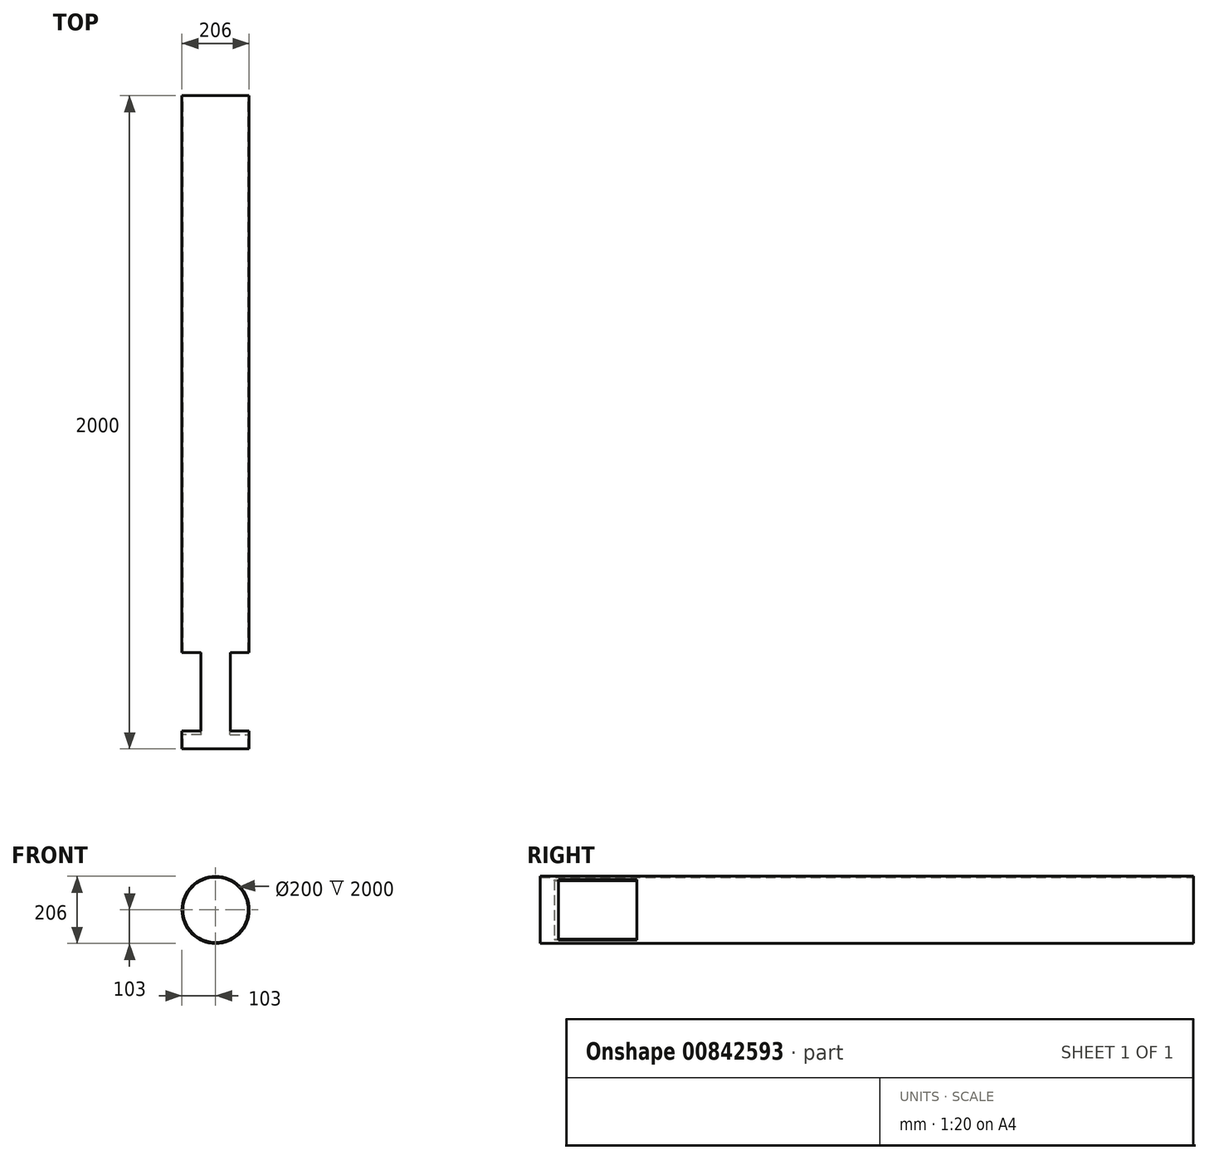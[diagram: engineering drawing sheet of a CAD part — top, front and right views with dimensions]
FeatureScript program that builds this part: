
annotation { "Feature Type Name" : "Feature", "Feature Type Description" : "" }
export const myFeature = defineFeature(function(context is Context, id is Id, definition is map)
    precondition{}
    {
        {
            var Q0;
            Q0=qCreatedBy(makeId("Front.planeOp"),FACE);
            var sketch = newSketch(context, id + "F0", { "sketchPlane" : qUnion([Q0])});
            skCircle(sketch, "E0", {"center": v(0, 0) * mm, "radius": 103 * mm});
            skCircle(sketch, "E1", {"center": v(0, 0) * mm, "radius": 100 * mm});
            skSolve(sketch);
        }
        {
            var Q0;
            Q0 = qSketchRegion(id + "F0", true);
            extrude(context, id + "F1", {"entities" : qUnion([Q0]), "depth" : 2000 * mm, "offsetDistance" : 25 * mm});
        }
        {
            var Q0;
            Q0=makeQuery(id+"F1.opExtrude","CAP_FACE",FACE,{"disambiguationData":[OSD([sQuery(id+"F0.wireOp",EDGE,"E0"),sQuery(id+"F0.wireOp",EDGE,"E1")])],"isStart":false});
            cPlane(context, id + "F2", {"entities" : qUnion([Q0]), "cplaneType" : CPlaneType.OFFSET, "offset" : 55 * mm, "oppositeDirection" : true, "width" : 150 * mm, "height" : 150 * mm});
        }
        {
            var Q0;
            Q0=qCreatedBy(id+"F2.planeOp",FACE);
            var sketch = newSketch(context, id + "F3", { "sketchPlane" : qUnion([Q0])});
            skArc(sketch, "E2", {"start": v(45.6, -93.47) * mm, "mid": v(104, 0) * mm, "end": v(45.6, 93.47) * mm});
            skArc(sketch, "E3.trimOffspring", {"start": v(-45.6, 93.47) * mm, "mid": v(-104, 0) * mm, "end": v(-45.6, -93.47) * mm});
            skLineSegment(sketch, "E4", {"start": v(-45.6, -93.47) * mm, "end": v(-14.63, -30) * mm});
            skLineSegment(sketch, "E5", {"start": v(45.6, -93.47) * mm, "end": v(14.63, -30) * mm});
            skLineSegment(sketch, "E6", {"start": v(-15.46, 31.7) * mm, "end": v(-45.6, 93.47) * mm});
            skLineSegment(sketch, "E7", {"start": v(15.46, 31.7) * mm, "end": v(45.6, 93.47) * mm});
            skLineSegment(sketch, "E8.bottom", {"start": v(15.46, 31.7) * mm, "end": v(-15.46, 31.7) * mm});
            skLineSegment(sketch, "E8.top", {"start": v(14.63, -30) * mm, "end": v(-14.63, -30) * mm});
            skPoint(sketch, "E8.middle", {"position": v(-0.41, 0.85) * mm});
            skSolve(sketch);
        }
        {
            var Q0;
            Q0 = qSketchRegion(id + "F3", true);
            extrude(context, id + "F4", {"entities" : qUnion([Q0]), "operationType" : NewBodyOperationType.REMOVE, "oppositeDirection" : true, "depth" : 240 * mm, "offsetDistance" : 25 * mm});
        }
        {
            var Q0;
            {var subQ0=sQuery(id+"F3.wireOp",EDGE,"E5");var subQ1=sQuery(id+"F3.wireOp",EDGE,"E7");Q0=makeQuery(id+"F4.boolean.opBoolean","COPY",FACE,{"disambiguationData":[TD([makeQuery(id+"F4.opExtrude","SWEPT_FACE",FACE,{"disambiguationData":[OSD([subQ0])]})])],"derivedFrom":makeQuery(id+"F4.opExtrude","CAP_FACE",FACE,{"disambiguationData":[OSD([sQuery(id+"F3.wireOp",EDGE,"E2"),sQuery(id+"F3.wireOp",EDGE,"E3.trimOffspring"),sQuery(id+"F3.wireOp",EDGE,"E4"),subQ0,sQuery(id+"F3.wireOp",EDGE,"E6"),subQ1,sQuery(id+"F3.wireOp",EDGE,"E8.bottom"),sQuery(id+"F3.wireOp",EDGE,"E8.top")])],"isStart":true})});}
            var sketch = newSketch(context, id + "F5", { "sketchPlane" : qUnion([Q0])});
            skLineSegment(sketch, "E9", {"start": v(-7.34, -15.06) * mm, "end": v(-44.5, -91.23) * mm});
            skLineSegment(sketch, "E10", {"start": v(-7.34, 15.06) * mm, "end": v(-44.5, 91.23) * mm});
            skLineSegment(sketch, "E11", {"start": v(7.34, -15.06) * mm, "end": v(44.5, -91.23) * mm});
            skLineSegment(sketch, "E12", {"start": v(7.34, 15.06) * mm, "end": v(44.5, 91.23) * mm});
            skPoint(sketch, "E13.middle", {"position": v(0, 0) * mm});
            skPoint(sketch, "E13.left.end.orphan", {"position": v(-19.04, -15.06) * mm});
            skPoint(sketch, "E14.orphan", {"position": v(-19.04, 15.06) * mm});
            skPoint(sketch, "E13.right.start.orphan", {"position": v(19.04, 15.06) * mm});
            skPoint(sketch, "E15.trimOffspring.end.orphan", {"position": v(19.04, -15.06) * mm});
            skLineSegment(sketch, "E16", {"start": v(-7.34, -15.06) * mm, "end": v(-7.34, 15.06) * mm});
            skLineSegment(sketch, "E17", {"start": v(7.34, 15.06) * mm, "end": v(7.34, -15.06) * mm});
            skArc(sketch, "E18", {"start": v(44.5, -91.23) * mm, "mid": v(101.5, 0) * mm, "end": v(44.5, 91.23) * mm});
            skArc(sketch, "E19.trimOffspring", {"start": v(-44.5, 91.23) * mm, "mid": v(-101.5, 0) * mm, "end": v(-44.5, -91.23) * mm});
            skSolve(sketch);
        }
        {
            var Q0;
            Q0 = qSketchRegion(id + "F5", true);
            extrude(context, id + "F6", {"entities" : qUnion([Q0]), "operationType" : NewBodyOperationType.REMOVE, "oppositeDirection" : true, "depth" : 12 * mm, "offsetDistance" : 25 * mm});
        }
    });
